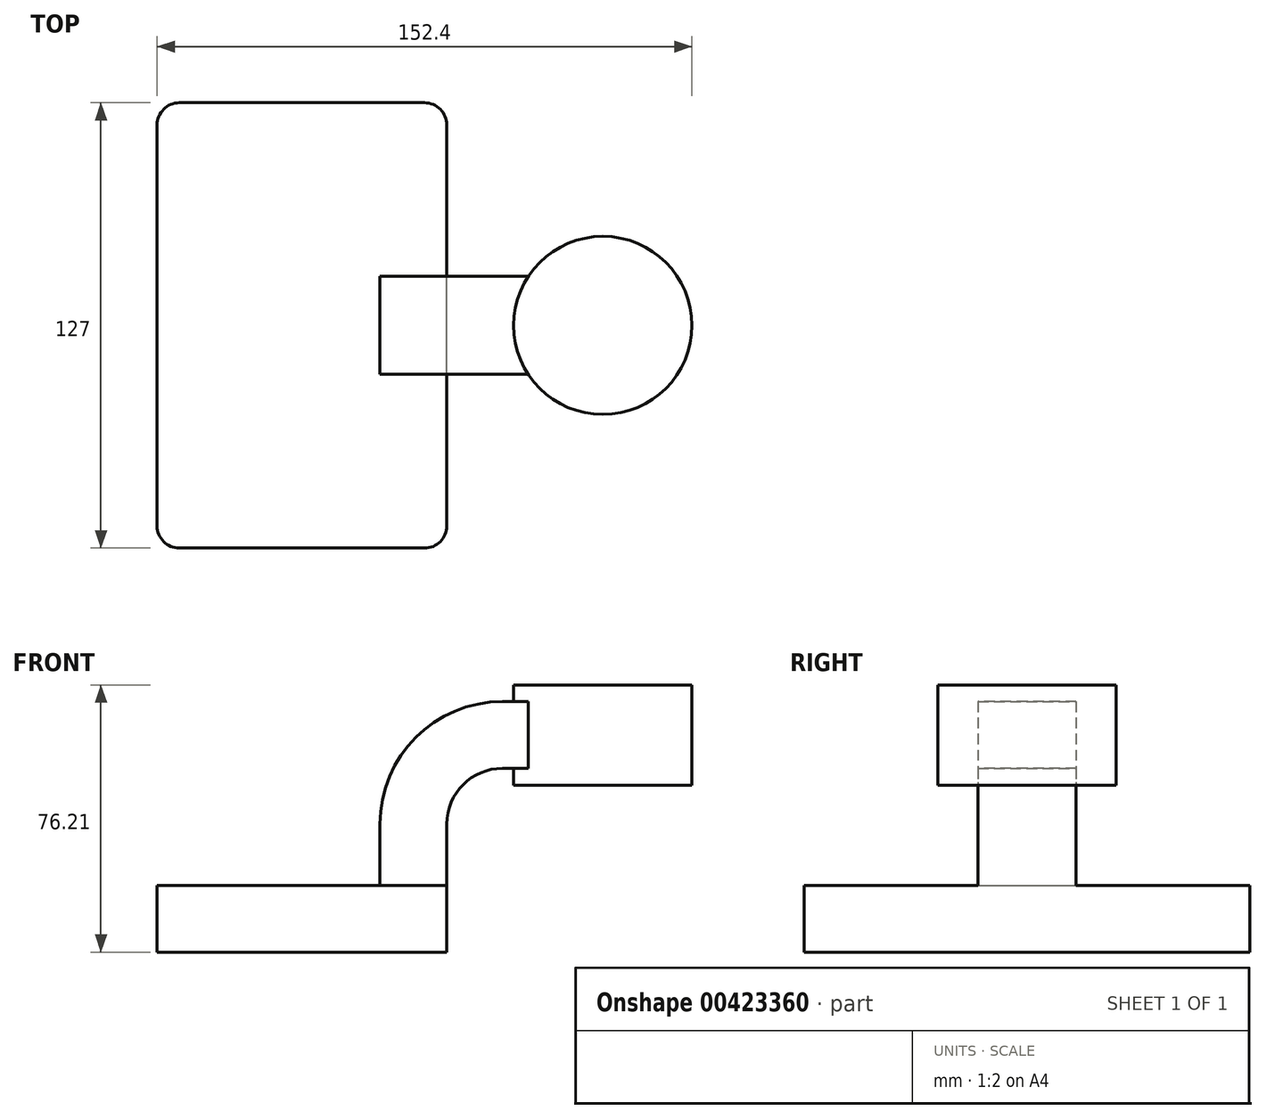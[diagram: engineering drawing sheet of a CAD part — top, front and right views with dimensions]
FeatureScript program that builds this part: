
annotation { "Feature Type Name" : "Feature", "Feature Type Description" : "" }
export const myFeature = defineFeature(function(context is Context, id is Id, definition is map)
    precondition{}
    {
        {
            var Q0;
            Q0=qCreatedBy(makeId("Front.planeOp"),FACE);
            var sketch = newSketch(context, id + "F0", { "sketchPlane" : qUnion([Q0])});
            skLineSegment(sketch, "E0.bottom", {"start": v(-41.27, -9.53) * mm, "end": v(41.28, -9.53) * mm});
            skLineSegment(sketch, "E0.top", {"start": v(-41.28, 9.52) * mm, "end": v(41.28, 9.52) * mm});
            skLineSegment(sketch, "E0.left", {"start": v(-41.28, -9.53) * mm, "end": v(-41.28, 9.52) * mm});
            skLineSegment(sketch, "E0.right", {"start": v(41.28, -9.53) * mm, "end": v(41.28, 9.52) * mm});
            skPoint(sketch, "E0.middle", {"position": v(0, 0) * mm});
            skLineSegment(sketch, "E1.bottom", {"start": v(60.33, 38.1) * mm, "end": v(111.12, 38.1) * mm});
            skLineSegment(sketch, "E1.top", {"start": v(60.32, 66.67) * mm, "end": v(111.12, 66.67) * mm});
            skLineSegment(sketch, "E1.left", {"start": v(60.33, 38.1) * mm, "end": v(60.32, 66.67) * mm});
            skLineSegment(sketch, "E1.right", {"start": v(111.12, 38.1) * mm, "end": v(111.12, 66.67) * mm});
            skPoint(sketch, "E1.middle", {"position": v(85.72, 52.39) * mm});
            skLineSegment(sketch, "E2", {"start": v(41.27, 9.52) * mm, "end": v(41.27, 27) * mm});
            skArc(sketch, "E3", {"start": v(41.27, 27) * mm, "mid": v(45.92, 38.23) * mm, "end": v(57.15, 42.88) * mm});
            skLineSegment(sketch, "E4", {"start": v(57.15, 42.88) * mm, "end": v(85.72, 42.88) * mm});
            skPoint(sketch, "E5", {"position": v(85.72, 38.1) * mm});
            skLineSegment(sketch, "E6.0", {"start": v(57.15, 61.93) * mm, "end": v(85.72, 61.93) * mm});
            skArc(sketch, "E6.1", {"start": v(22.22, 27) * mm, "mid": v(32.45, 51.7) * mm, "end": v(57.15, 61.93) * mm});
            skLineSegment(sketch, "E6.2", {"start": v(22.22, 9.52) * mm, "end": v(22.22, 27) * mm});
            skLineSegment(sketch, "E7", {"start": v(85.72, 38.1) * mm, "end": v(85.72, 66.67) * mm});
            skFitSpline(sketch, "E8", {"points": [v(-41.28, 9.53) * mm, v(57.15, 61.93) * mm], "startDerivative": vector(1.25, 79.25) * mm, "endDerivative": vector(90.78, -4.45) * mm});
            skSolve(sketch);
        }
        {
            var Q0;
            Q0=makeQuery(id+"F0.imprint","IMPRINT",FACE,{"disambiguationData":[TD([[makeQuery(id+"F0.imprint","IMPRINT",EDGE,{"derivedFrom":sQuery(id+"F0.wireOp",EDGE,"E0.bottom")}),1.0]])]});
            extrude(context, id + "F1", {"entities" : qUnion([Q0]), "endBound" : BoundingType.SYMMETRIC, "depth" : 127 * mm});
        }
        {
            var Q0;
            {var subQ1=sQuery(id+"F0.wireOp",EDGE,"E2");Q0=makeQuery(id+"F0.imprint","IMPRINT",FACE,{"disambiguationData":[TD([[makeQuery(id+"F0.imprint","IMPRINT",EDGE,{"derivedFrom":subQ1}),1.0]])]});}
            var Q1;
            {var subQ0=sQuery(id+"F0.wireOp",EDGE,"E4");var subQ1=sQuery(id+"F0.wireOp",EDGE,"E1.left");var subQ2=makeQuery(id+"F0.imprint","INTERSECT",VERTEX,{"derivedFrom":[subQ1,subQ0]});Q1=makeQuery(id+"F0.imprint","IMPRINT",FACE,{"disambiguationData":[TD([[makeQuery(id+"F0.imprint","IMPRINT",EDGE,{"disambiguationData":[TD([[subQ2,-1.0]])],"derivedFrom":subQ1}),-1.0]])]});}
            extrude(context, id + "F2", {"entities" : qUnion([Q0, Q1]), "operationType" : NewBodyOperationType.ADD, "endBound" : BoundingType.SYMMETRIC, "depth" : 27.94 * mm});
        }
        {
            var Q0;
            Q0=makeQuery(id+"F0.imprint","IMPRINT",FACE,{"disambiguationData":[TD([[makeQuery(id+"F0.imprint","IMPRINT",EDGE,{"derivedFrom":sQuery(id+"F0.wireOp",EDGE,"E6.1")}),1.0]])]});
            extrude(context, id + "F3", {"entities" : qUnion([Q0]), "operationType" : NewBodyOperationType.ADD, "endBound" : BoundingType.SYMMETRIC, "depth" : 15.88 * mm});
        }
        {
            var Q0;
            {var subQ0=sQuery(id+"F0.wireOp",EDGE,"E1.right");Q0=makeQuery(id+"F0.imprint","IMPRINT",FACE,{"disambiguationData":[TD([[makeQuery(id+"F0.imprint","IMPRINT",EDGE,{"derivedFrom":subQ0}),1.0]])]});}
            var Q1;
            Q1=sQuery(id+"F0.wireOp",EDGE,"E7");
            revolve(context, id + "F4", {"operationType" : NewBodyOperationType.ADD, "entities" : qUnion([Q0]), "axis" : qUnion([Q1]), "revolveType" : RevolveType.FULL});
        }
        {
            var Q0;
            Q0=makeQuery(id+"F1.opExtrude","CAP_EDGE",EDGE,{"disambiguationData":[OSD([sQuery(id+"F0.wireOp",EDGE,"E0.right")])],"isStart":false});
            var Q1;
            Q1=makeQuery(id+"F1.opExtrude","CAP_EDGE",EDGE,{"disambiguationData":[OSD([sQuery(id+"F0.wireOp",EDGE,"E0.left")])],"isStart":false});
            var Q2;
            Q2=makeQuery(id+"F1.opExtrude","CAP_EDGE",EDGE,{"disambiguationData":[OSD([sQuery(id+"F0.wireOp",EDGE,"E0.left")])],"isStart":true});
            var Q3;
            Q3=makeQuery(id+"F1.opExtrude","CAP_EDGE",EDGE,{"disambiguationData":[OSD([sQuery(id+"F0.wireOp",EDGE,"E0.right")])],"isStart":true});
            fillet(context, id + "F5", {"entities" : qUnion([Q0, Q1, Q2, Q3]), "radius" : 6.35 * mm, "tangentPropagation" : true, "allowEdgeOverflow" : false});
        }
    });
